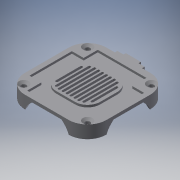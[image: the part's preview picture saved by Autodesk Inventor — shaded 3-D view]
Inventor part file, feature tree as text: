
AUTODESK INVENTOR PART (.ipt)
format: ipt  version: 2018 (Build 220112000, 112)  size: 599,040 bytes
history: native  units: mm
features: reference x24, extrude x7, sketch x6, projected_geometry x5, chamfer x4, fillet x3, other x3, plane x1
ambient origin geometry x8: Origin, YZ Plane, XZ Plane, XY Plane, X Axis, Y Axis, Z Axis, Center Point
bodies: Volumenkörper1 (feature_tree)
feature tree (53):
  extrude  "Extrusion1"  Depth=2.5mm TaperAngle=0.0deg
  extrude  "Extrusion2"  Depth=3.0mm
  sketch  "Skizze3"  dims[d9=30.0mm d10=6.0mm]
  sketch  "Skizze4"  dims[d11=6.0mm d13=6.0mm]
  plane  "Arbeitsebene1"
  extrude  "Extrusion3"  Depth=6.0mm
  extrude  "Extrusion4"  Depth=6.0mm
  chamfer  "Fase1"  Distance=6.4mm
  extrude  "Extrusion5"  Depth=1.25mm TaperAngle=45.0deg
  fillet  "Rundung1"  Radius=9.0mm
  chamfer  "Fase3"  Distance=9.0mm
  fillet  "Rundung2"  Radius=9.0mm
  chamfer  "Fase4"  Distance=9.0mm
  extrude  "Extrusion6"  Depth=1.25mm
  fillet  "Rundung3"  Radius=3.0mm
  chamfer  "Fase5"  Distance=13.0mm
  extrude  "Extrusion7"  Depth=1.25mm
  sketch  "Skizze1"  dims[d0=2.0mm d1=0.0mm d4=2.5mm d5=0.0mm]
  reference  "Referenz1"
  reference  "Referenz2"
  reference  "Referenz3"
  reference  "Referenz4"
  reference  "Referenz5"
  reference  "Referenz6"
  reference  "Referenz7"
  reference  "Referenz8"
  reference  "Referenz9"
  reference  "Referenz10"
  sketch  "Skizze2"  dims[d7=3.0mm d8=3.0mm]
  reference  "Referenz12"
  reference  "Referenz13"
  reference  "Referenz14"
  reference  "Referenz15"
  projected_geometry  "Projizierte Kontur1"
  projected_geometry  "Projizierte Kontur2"
  sketch  "Skizze5"  dims[d14=6.0mm d15=6.4mm d16=0.0mm]
  sketch  "Skizze6"  dims[d17=33.0mm d18=0.0mm d19=1.4mm d20=2.0mm d21=45.0deg d22=9.0mm d23=9.0mm d24=9.0mm d25=9.0mm d26=3.0mm d27=3.0mm d28=13.0mm d29=13.0mm d30=27.0mm d31=4.0mm d32=3.0mm d33=31.0mm d34=10.5mm d35=10.5mm d36=10.5mm d37=31.0mm d38=10.5mm d39=1.4mm d40=0.0mm d41=8.0mm d45=4.5mm d46=2.0mm d47=45.0deg d48=11.75mm d49=1.5mm d50=1.5mm d51=1.5mm d52=0.5mm d54=1.0mm d55=1.5mm d56=1.5mm d57=1.5mm d58=1.5mm d59=1.5mm d60=1.5mm d61=1.5mm d62=1.5mm d63=1.0mm d64=1.0mm d65=1.0mm d66=1.0mm d67=1.0mm d68=1.0mm d69=1.0mm d70=1.0mm d72=7.1mm d73=0.0mm d74=8.0mm d75=1.75mm d76=45.0deg d77=0.5mm d78=0.2mm d79=1.75mm d80=45.0deg d82=0.25mm d86=0.2mm d87=0.2mm d88=0.2mm d89=0.2mm d90=0.2mm d91=4.051543mm d92=1.5mm d93=1.25mm d94=0.0mm]
  projected_geometry  "Projizierte Kontur3"
  reference  "Referenz17"
  reference  "Referenz18"
  reference  "Referenz19"
  reference  "Referenz23"
  reference  "Referenz24"
  reference  "Referenz25"
  reference  "Referenz26"
  reference  "Referenz27"
  reference  "Referenz28"
  reference  "Referenz29"
  projected_geometry  "Projizierte Kontur4"
  projected_geometry  "Projizierte Kontur5"
  parser-record x1  (decoder bookkeeping rows leaked as tree rows — omitted from the tree; the rows remain in map.json)
  other  "VolumeKnob.iam"
  other  "Oberbau:1"
note: 1 file-system path scrubbed to <path> (originals preserved in map.json)
